FCSTD DOCUMENT  (FreeCAD 0.19R0.19.2)
Label: v0_09
License: All rights reserved
LicenseURL: http://en.wikipedia.org/wiki/All_rights_reserved
objects: Sketcher::SketchObject×1
note: 1 computed .brp shape members not serialized (recipe doc carries the construction recipe); baked Part::Feature solids carry a one-line shape summary decoded from their .brp

FEATURE [Sketcher::SketchObject] Sketch
  FullyConstrained = true
  sketch-geometry (35):
    g0: LineSegment StartX=0 StartY=0 StartZ=0 EndX=154.4 EndY=0 EndZ=0
    g1: LineSegment StartX=154.4 StartY=0 StartZ=0 EndX=154.4 EndY=-7 EndZ=0
    g2: LineSegment StartX=154.9 StartY=-7.5 StartZ=0 EndX=161.9 EndY=-7.5 EndZ=0
    g3: ArcOfCircle CenterX=154.9 CenterY=-7 CenterZ=0 NormalX=0 NormalY=0 NormalZ=1 AngleXU=0 Radius=0.5 StartAngle=3.14159 EndAngle=4.71239
    g4: LineSegment StartX=154.4 StartY=0 StartZ=0 EndX=121.35 EndY=0 EndZ=0
    g5: LineSegment StartX=121.35 StartY=0 StartZ=0 EndX=121.35 EndY=-11.9 EndZ=0
    g6: Circle CenterX=121.35 CenterY=-11.9 CenterZ=0 NormalX=0 NormalY=0 NormalZ=1 AngleXU=0 Radius=3.25
    g7: LineSegment StartX=0 StartY=0 StartZ=0 EndX=0 EndY=-4 EndZ=0
    g8: LineSegment StartX=-5 StartY=-4 StartZ=0 EndX=0 EndY=-4 EndZ=0
    g9: LineSegment StartX=-5 StartY=-4 StartZ=0 EndX=-5 EndY=-6.5 EndZ=0
    g10: LineSegment StartX=-7.5 StartY=-9 StartZ=0 EndX=-7.5 EndY=-12.75 EndZ=0
    g11: ArcOfCircle CenterX=-5 CenterY=-9 CenterZ=0 NormalX=0 NormalY=0 NormalZ=1 AngleXU=0 Radius=2.5 StartAngle=1.5708 EndAngle=3.14159
    g12: LineSegment StartX=-5 StartY=-15.25 StartZ=0 EndX=-2.5 EndY=-15.25 EndZ=0
    g13: ArcOfCircle CenterX=-5 CenterY=-12.75 CenterZ=0 NormalX=0 NormalY=0 NormalZ=1 AngleXU=0 Radius=2.5 StartAngle=3.14159 EndAngle=4.71239
    g14: LineSegment StartX=-2.5 StartY=-15.25 StartZ=0 EndX=-2.5 EndY=-12.75 EndZ=0
    g15: LineSegment StartX=-2.5 StartY=-12.75 StartZ=0 EndX=1.488e-13 EndY=-12.75 EndZ=0
    g16: ArcOfCircle CenterX=1.486e-13 CenterY=-15.25 CenterZ=0 NormalX=0 NormalY=0 NormalZ=1 AngleXU=0 Radius=2.5 StartAngle=8e-16 EndAngle=1.5708
    g17: LineSegment StartX=2.5 StartY=-15.25 StartZ=0 EndX=2.5 EndY=-19 EndZ=0
    g18: ArcOfCircle CenterX=1.483e-13 CenterY=-19 CenterZ=0 NormalX=0 NormalY=0 NormalZ=1 AngleXU=0 Radius=2.5 StartAngle=4.71239 EndAngle=6.28319
    g19: LineSegment StartX=-2.5 StartY=-21.5 StartZ=0 EndX=1.479e-13 EndY=-21.5 EndZ=0
    g20: LineSegment StartX=-2.5 StartY=-21.5 StartZ=0 EndX=-2.5 EndY=-24 EndZ=0
    g21: LineSegment StartX=-7.5 StartY=-24 StartZ=0 EndX=-2.5 EndY=-24 EndZ=0
    g22: LineSegment StartX=-7.5 StartY=-24 StartZ=0 EndX=-7.5 EndY=-28 EndZ=0
    g23: LineSegment StartX=161.9 StartY=-7.5 StartZ=0 EndX=161.9 EndY=-36 EndZ=0
    g24: LineSegment StartX=61.85 StartY=-36 StartZ=0 EndX=161.9 EndY=-36 EndZ=0
    g25-g29: Circle x5 (B-spline internal-alignment scaffolding for g30; pole/knot coordinates omitted)
    g30: BSplineCurve PolesCount=5 KnotsCount=3 Degree=3 IsPeriodic=0
    g31: GeomPoint X=61.85 Y=-36 Z=0
    g32: GeomPoint X=47.2264 Y=-32.2128 Z=0
    g33: GeomPoint X=32.5209 Y=-28 Z=0
    g34: LineSegment StartX=32.5209 StartY=-28 StartZ=0 EndX=-7.5 EndY=-28 EndZ=0
  constraints (83):
    c: PointOnObject(g0,g-2)
    c: Horizontal(g0)
    c: Distance(g0) = 154.4
    c: DistanceY(g-1,g0) = 0
    c: Vertical(g1)
    c: Distance(g1) = 7
    c: Coincident(g1,g0)
    c: Horizontal(g2)
    c: Distance(g2) = 7
    c: Coincident(g3,g1)
    c: Tangent(g1,g3) = -1.5708
    c: Tangent(g2,g3)
    c: Tangent(g2,g3,g2) = -1.5708
    c: Block(g3)
    c: Horizontal(g4)
    c: Distance(g4) = 33.05
    c: Coincident(g4,g0)
    c: Vertical(g5)
    c: Distance(g5) = 11.9
    c: Coincident(g5,g4)
    c: Coincident(g6,g5)
    c: Block(g6)
    c: Vertical(g7)
    c: Distance(g7) = 4
    c: Coincident(g7,g0)
    c: Horizontal(g8)
    c: Distance(g8) = 5
    c: Coincident(g8,g7)
    c: Vertical(g9)
    c: Distance(g9) = 2.5
    c: Coincident(g9,g8)
    c: Vertical(g10)
    c: Distance(g10) = 3.75
    c: Coincident(g11,g9)
    c: Block(g11)
    c: Coincident(g10,g11)
    c: Horizontal(g12)
    c: Distance(g12) = 2.5
    c: Coincident(g13,g10)
    c: Block(g13)
    c: Block(g12)
    c: Vertical(g14)
    c: Distance(g14) = 2.5
    c: Coincident(g14,g12)
    c: Horizontal(g15)
    c: Distance(g15) = 2.5
    c: Coincident(g15,g14)
    c: Coincident(g16,g15)
    c: Vertical(g17)
    c: Distance(g17) = 3.75
    c: Block(g16)
    c: Coincident(g17,g16)
    c: Coincident(g18,g17)
    c: Block(g18)
    c: Horizontal(g19)
    c: Distance(g19) = 2.5
    c: Coincident(g19,g18)
    c: Vertical(g20)
    c: Distance(g20) = 2.5
    c: Coincident(g20,g19)
    c: Horizontal(g21)
    c: Distance(g21) = 5
    c: Coincident(g21,g20)
    c: Vertical(g22)
    c: Distance(g22) = 4
    c: Coincident(g22,g21)
    c: Vertical(g23)
    c: Distance(g23) = 28.5
    c: Coincident(g23,g2)
    c: Horizontal(g24)
    c: Distance(g24) = 100.05
    c: Coincident(g24,g23)
    c: Coincident(g30,g24)
    c: Weight(g25) = 1
    c: Equal(g25, g26-g29) x4
    c: InternalAlignment(g25-g29 -> g30) x5
    c: InternalAlignment(g31,g30)
    c: InternalAlignment(g32,g30)
    c: InternalAlignment(g33,g30)
    c: Horizontal(g34)
    c: Coincident(g34,g22)
    c: Coincident(g34,g30)
    c: Block(g30)
